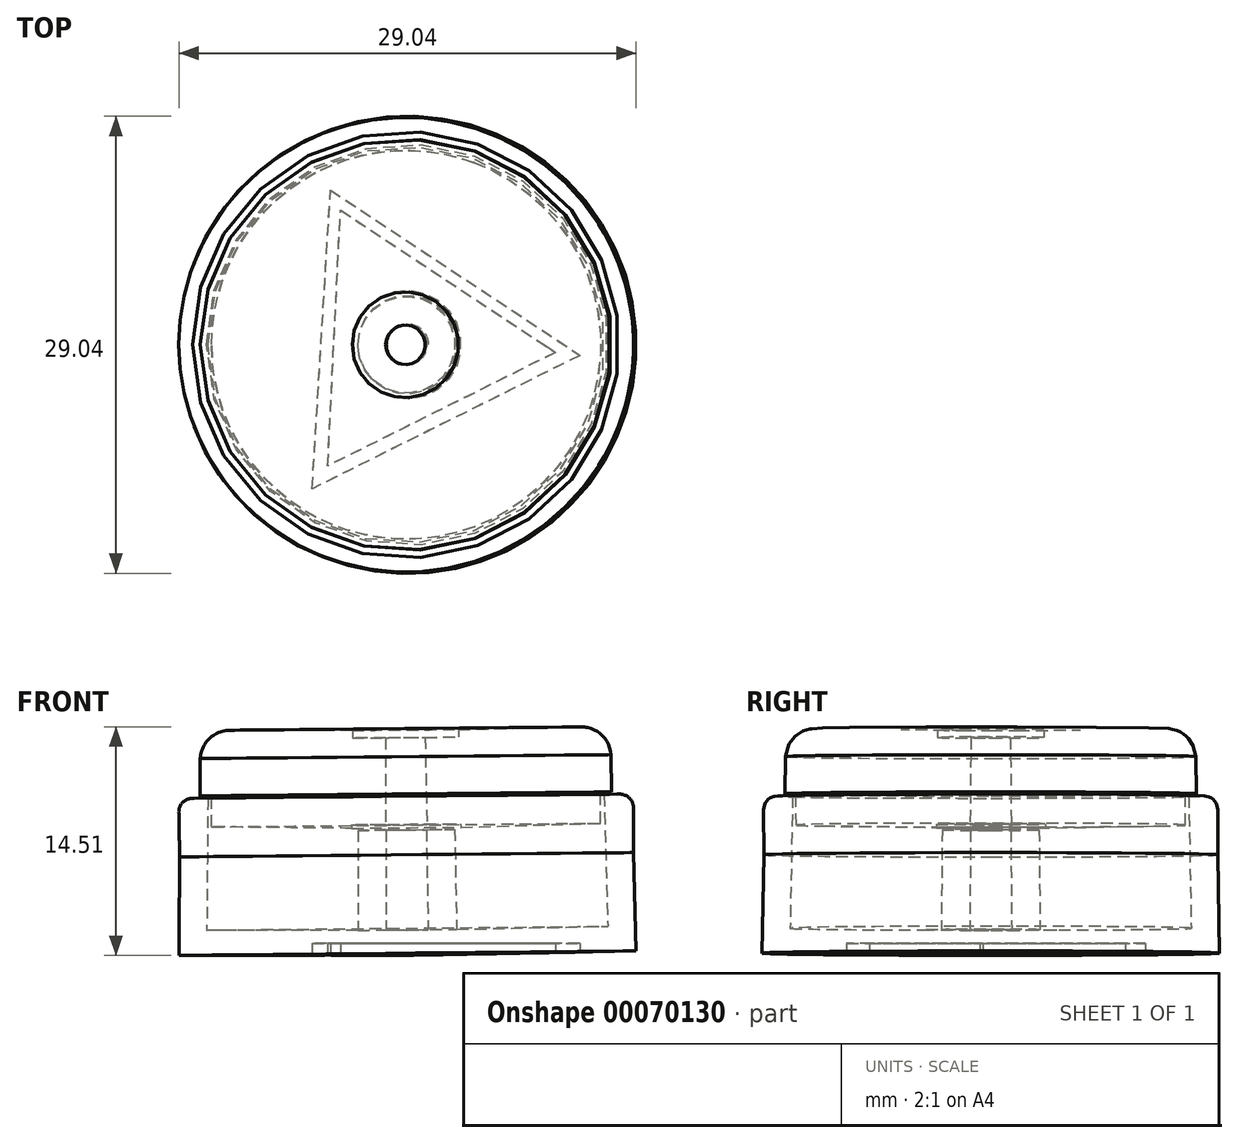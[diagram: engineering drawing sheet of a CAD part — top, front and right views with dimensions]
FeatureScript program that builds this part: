
annotation { "Feature Type Name" : "Feature", "Feature Type Description" : "" }
export const myFeature = defineFeature(function(context is Context, id is Id, definition is map)
    precondition{}
    {
        {
            var Q0;
            Q0=qCreatedBy(makeId("Front.planeOp"),FACE);
            var sketch = newSketch(context, id + "F0", { "sketchPlane" : qUnion([Q0])});
            skLineSegment(sketch, "E0", {"start": v(-3.15, 7.94) * mm, "end": v(-3.15, 1.6) * mm});
            skLineSegment(sketch, "E1", {"start": v(-1.35, 7.95) * mm, "end": v(-1.35, 1.6) * mm});
            skLineSegment(sketch, "E2", {"start": v(-1.35, 7.95) * mm, "end": v(-3.15, 7.94) * mm});
            skLineSegment(sketch, "E3", {"start": v(-12.68, 9.98) * mm, "end": v(-12.75, 1.6) * mm});
            skLineSegment(sketch, "E4", {"start": v(-14.52, 9.1) * mm, "end": v(-14.47, 6.25) * mm});
            skLineSegment(sketch, "E5", {"start": v(-14.47, 6.25) * mm, "end": v(-14.52, 0) * mm});
            skLineSegment(sketch, "E6", {"start": v(0, 0) * mm, "end": v(-14.52, 0) * mm});
            skLineSegment(sketch, "E7", {"start": v(-3.15, 1.6) * mm, "end": v(-12.75, 1.6) * mm});
            skLineSegment(sketch, "E8", {"start": v(-0.02, 1.6) * mm, "end": v(-1.35, 1.6) * mm});
            skLineSegment(sketch, "E9", {"start": v(0, 0) * mm, "end": v(-0.02, 1.6) * mm});
            skArc(sketch, "E10", {"start": v(-13.64, 9.98) * mm, "mid": v(-14.27, 9.72) * mm, "end": v(-14.52, 9.1) * mm});
            skLineSegment(sketch, "E11", {"start": v(-12.68, 9.98) * mm, "end": v(-13.64, 9.98) * mm});
            skLineSegment(sketch, "E12", {"start": v(-3.18, 9.2) * mm, "end": v(0, 9.2) * mm, "construction": true});
            skSolve(sketch);
        }
        {
            var Q0;
            Q0=qCreatedBy(makeId("Front.planeOp"),FACE);
            var sketch = newSketch(context, id + "F1", { "sketchPlane" : qUnion([Q0])});
            skLineSegment(sketch, "E13", {"start": v(-3.54, 8.07) * mm, "end": v(-12.43, 8.16) * mm});
            skLineSegment(sketch, "E14", {"start": v(-3.54, 8.3) * mm, "end": v(-3.54, 8.07) * mm});
            skLineSegment(sketch, "E15", {"start": v(-13.16, 12.5) * mm, "end": v(-13.16, 10.13) * mm});
            skArc(sketch, "E16", {"start": v(-11.27, 14.3) * mm, "mid": v(-12.57, 13.77) * mm, "end": v(-13.16, 12.5) * mm});
            skLineSegment(sketch, "E17", {"start": v(-11.27, 14.3) * mm, "end": v(-3.5, 14.28) * mm});
            skLineSegment(sketch, "E18", {"start": v(-3.5, 14.28) * mm, "end": v(-3.5, 13.8) * mm});
            skLineSegment(sketch, "E19", {"start": v(-12.45, 10.14) * mm, "end": v(-13.16, 10.13) * mm});
            skLineSegment(sketch, "E20", {"start": v(-3.54, 8.3) * mm, "end": v(-1.39, 8.3) * mm});
            skLineSegment(sketch, "E21", {"start": v(-1.39, 8.3) * mm, "end": v(-1.39, 13.82) * mm});
            skLineSegment(sketch, "E22", {"start": v(-3.5, 13.8) * mm, "end": v(-1.39, 13.82) * mm});
            skLineSegment(sketch, "E23", {"start": v(-12.43, 8.16) * mm, "end": v(-12.45, 10.14) * mm});
            skSolve(sketch);
        }
        {
            var Q0;
            Q0=qSketchRegion(id+"F0",true);
            var Q1;
            Q1=sQuery(id+"F0.wireOp",EDGE,"E9");
            revolve(context, id + "F2", {"entities" : qUnion([Q0]), "axis" : qUnion([Q1]), "revolveType" : RevolveType.FULL});
        }
        {
            var Q0;
            Q0=qSketchRegion(id+"F1",true);
            var Q1;
            Q1=sQuery(id+"F0.wireOp",EDGE,"E9");
            revolve(context, id + "F3", {"entities" : qUnion([Q0]), "axis" : qUnion([Q1]), "revolveType" : RevolveType.FULL});
        }
        {
            var Q0;
            Q0=qCreatedBy(makeId("Top.planeOp"),FACE);
            var sketch = newSketch(context, id + "F4", { "sketchPlane" : qUnion([Q0])});
            skCircle(sketch, "E24.cCircle", {"center": v(0, 0) * mm, "radius": 5.48 * mm, "construction": true});
            skLineSegment(sketch, "E24.0", {"start": v(10.95, -0.67) * mm, "end": v(-6.05, -9.15) * mm});
            skLineSegment(sketch, "E24.1", {"start": v(-6.05, -9.15) * mm, "end": v(-4.9, 9.82) * mm});
            skLineSegment(sketch, "E24.2", {"start": v(-4.9, 9.82) * mm, "end": v(10.95, -0.67) * mm});
            skPoint(sketch, "E24.0.midPoint", {"position": v(2.45, -4.9) * mm});
            skPoint(sketch, "E25.0.midPoint", {"position": v(-2.64, 4.35) * mm});
            skLineSegment(sketch, "E26", {"start": v(-4.26, 8.55) * mm, "end": v(9.39, -0.48) * mm});
            skLineSegment(sketch, "E27", {"start": v(9.39, -0.48) * mm, "end": v(-5.06, -7.7) * mm});
            skLineSegment(sketch, "E28", {"start": v(-5.06, -7.7) * mm, "end": v(-4.26, 8.55) * mm});
            skSolve(sketch);
        }
        {
            var Q0;
            Q0 = qSketchRegion(id + "F4", true);
            extrude(context, id + "F5", {"entities" : qUnion([Q0]), "operationType" : NewBodyOperationType.REMOVE, "depth" : .75 * mm});
        }
    });
